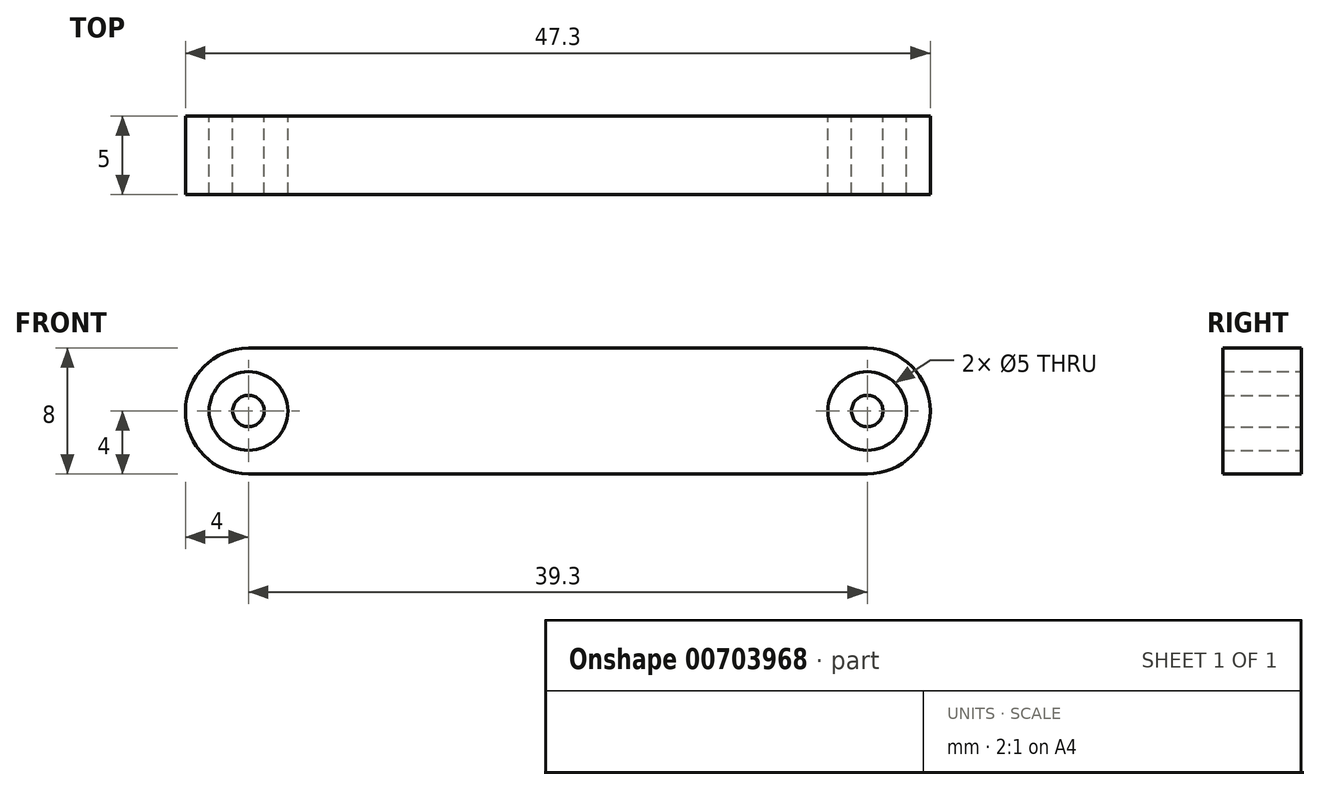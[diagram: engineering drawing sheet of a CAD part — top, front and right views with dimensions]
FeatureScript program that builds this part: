
annotation { "Feature Type Name" : "Feature", "Feature Type Description" : "" }
export const myFeature = defineFeature(function(context is Context, id is Id, definition is map)
    precondition{}
    {
        {
            var Q0;
            Q0=qCreatedBy(makeId("Front.planeOp"),FACE);
            var sketch = newSketch(context, id + "F0", { "sketchPlane" : qUnion([Q0])});
            skLineSegment(sketch, "E0.bottom", {"start": v(0, 0) * mm, "end": v(39.3, 0) * mm});
            skLineSegment(sketch, "E0.top", {"start": v(0, 8) * mm, "end": v(39.3, 8) * mm});
            skArc(sketch, "E1", {"start": v(39.3, 0) * mm, "mid": v(43.3, 4) * mm, "end": v(39.3, 8) * mm});
            skArc(sketch, "E2", {"start": v(0, 8) * mm, "mid": v(-4, 4) * mm, "end": v(0, 0) * mm});
            skCircle(sketch, "E3", {"center": v(0, 4) * mm, "radius": 2.5 * mm});
            skCircle(sketch, "E4", {"center": v(0, 4) * mm, "radius": 1 * mm});
            skCircle(sketch, "E5", {"center": v(39.3, 4) * mm, "radius": 2.5 * mm});
            skCircle(sketch, "E6", {"center": v(39.3, 4) * mm, "radius": 1 * mm});
            skSolve(sketch);
        }
        {
            var Q0;
            Q0 = qSketchRegion(id + "F0", true);
            var Q1;
            Q1=makeQuery(id+"F0.imprint","IMPRINT",FACE,{"disambiguationData":[TD([[makeQuery(id+"F0.imprint","IMPRINT",EDGE,{"derivedFrom":sQuery(id+"F0.wireOp",EDGE,"E4")}),1.0]])]});
            var Q2;
            Q2=makeQuery(id+"F0.imprint","IMPRINT",FACE,{"disambiguationData":[TD([[makeQuery(id+"F0.imprint","IMPRINT",EDGE,{"derivedFrom":sQuery(id+"F0.wireOp",EDGE,"E6")}),1.0]])]});
            extrude(context, id + "F1", {"entities" : qUnion([Q0, Q1, Q2]), "depth" : 5 * mm, "offsetDistance" : 25 * mm});
        }
    });
